# Revit family: 14 LIGHT Panca
name_source: partatom
category: Arredi
units: mm (PartAtom-declared; Revit-internal decimal feet)

## family parameters
Basato su piano di lavoro = Sì
Condiviso = No
Punto di calcolo locali = No
Sempre verticale = Sì
Taglio con vuoti quando caricato = No

## types (16) — shared parameters
Imbottiture = 3518_Luxy_Imbottiture
Prospetto di default = 1219 mm
Struttura = 3518_Luxy_Struttura

## per-type parameters (varying)
| type | Braccioli | Laterale | Mod_16000 | dist_gamba_cen | gamba | lunghezza | modulo | num_sedute |
| 16000 2P_4PA1602 | No | 266 mm  [stored 0.872703 ft] | Sì | 505 mm | No | 1037 mm | 505 mm | 2 |
| 16000 3P_4PA1604 | No | 266 mm  [stored 0.872703 ft] | Sì | 1023 mm | No | 1541 mm  [stored 5.05577 ft] | 505 mm | 3 |
| 16000 4P_4PA1606 | No | 266 mm  [stored 0.872703 ft] | Sì | 1023 mm | No | 2046 mm | 505 mm | 4 |
| 16000 5P_4PA1608 | No | 266 mm  [stored 0.872703 ft] | Sì | 1023 mm | Sì | 2550 mm  [stored 8.36614 ft] | 505 mm | 5 |
| 16000B 2P_4PA1603 | Sì | 306 mm | Sì | 585 mm  [stored 1.91929 ft] | No | 1196 mm  [stored 3.92388 ft] | 585 mm  [stored 1.91929 ft] | 2 |
| 16000B 3P_4PA1605 | Sì | 306 mm | Sì | 1183 mm  [stored 3.88123 ft] | No | 1781 mm  [stored 5.84318 ft] | 585 mm  [stored 1.91929 ft] | 3 |
| 16000B 4P_4PA1607 | Sì | 306 mm | Sì | 1183 mm  [stored 3.88123 ft] | No | 2366 mm  [stored 7.76247 ft] | 585 mm  [stored 1.91929 ft] | 4 |
| 16000B 5P_4PA1609 | Sì | 306 mm | Sì | 1183 mm  [stored 3.88123 ft] | Sì | 2951 mm  [stored 9.68176 ft] | 585 mm  [stored 1.91929 ft] | 5 |
| 14000 2P_4PA1402 | No | 266 mm  [stored 0.872703 ft] | No | 505 mm | No | 1037 mm | 505 mm | 2 |
| 14000 3P_4PA1404 | No | 266 mm  [stored 0.872703 ft] | No | 1023 mm | No | 1541 mm  [stored 5.05577 ft] | 505 mm | 3 |
| 14000 4P_4PA1406 | No | 266 mm  [stored 0.872703 ft] | No | 1023 mm | No | 2046 mm | 505 mm | 4 |
| 14000 5P_4PA1408 | No | 266 mm  [stored 0.872703 ft] | No | 1023 mm | No | 2046 mm | 505 mm | 4 |
| 14000B 2P_4PA1403 | Sì | 306 mm | No | 1183 mm  [stored 3.88123 ft] | No | 2366 mm  [stored 7.76247 ft] | 585 mm  [stored 1.91929 ft] | 4 |
| 14000B 3P_4PA1405 | Sì | 306 mm | No | 1183 mm  [stored 3.88123 ft] | No | 2366 mm  [stored 7.76247 ft] | 585 mm  [stored 1.91929 ft] | 4 |
| 14000B 4P_4PA1407 | Sì | 306 mm | No | 1183 mm  [stored 3.88123 ft] | No | 2366 mm  [stored 7.76247 ft] | 585 mm  [stored 1.91929 ft] | 4 |
| 14000B 5P_4PA1409 | Sì | 306 mm | No | 1183 mm  [stored 3.88123 ft] | Sì | 2951 mm  [stored 9.68176 ft] | 585 mm  [stored 1.91929 ft] | 5 |

note: [stored X ft] marks values corroborated as IEEE doubles in the binary element streams (Revit-internal decimal feet)

## geometry (parser evidence)
native form markers: Sweep x9
no freeform markers — native parametric forms only
